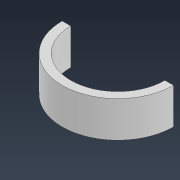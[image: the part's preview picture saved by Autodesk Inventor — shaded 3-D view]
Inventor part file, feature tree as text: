
AUTODESK INVENTOR PART (.ipt)
format: ipt  version: 2022 (Build 260153000, 153)  size: 82,944 bytes
history: native  units: mm
features: extrude x1, sketch x1
ambient origin geometry x8: Origin, YZ Plane, XZ Plane, XY Plane, X Axis, Y Axis, Z Axis, Center Point
bodies: Solid1 (feature_tree)
feature tree (2):
  extrude  "Extrusion1"  Depth=21.0mm
  sketch  "Sketch1"  dims[d0=55.0mm d1=65.0mm d2=21.0mm d3=0.0mm]
